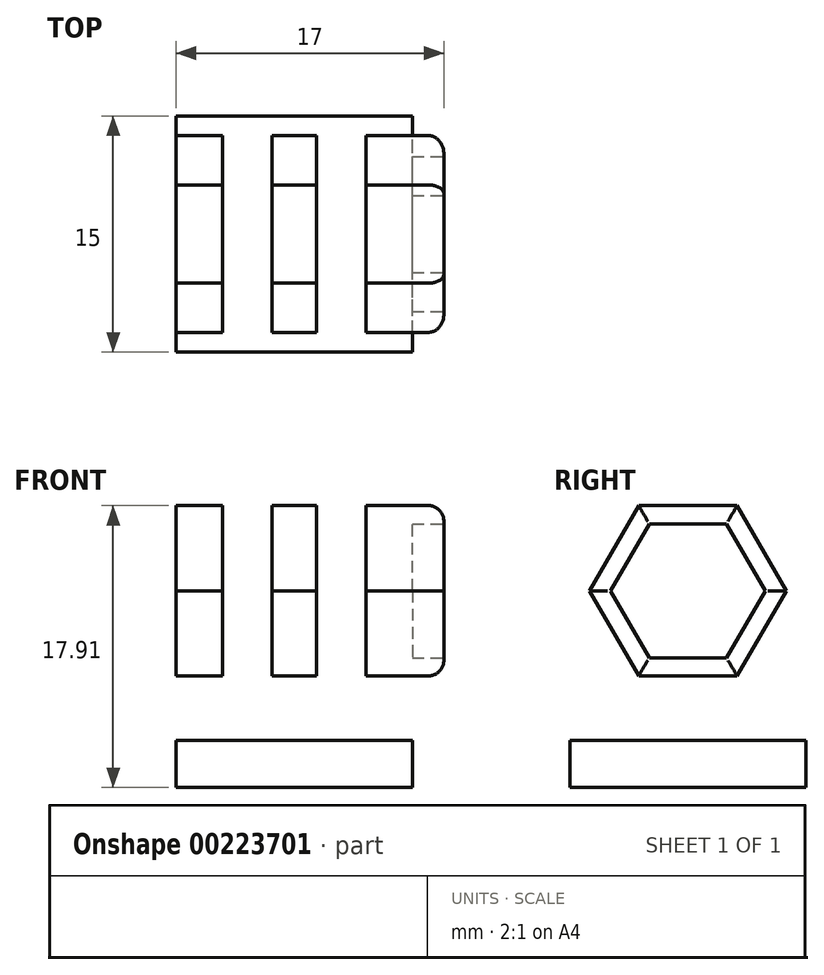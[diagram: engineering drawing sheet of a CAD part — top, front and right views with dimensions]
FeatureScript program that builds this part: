
annotation { "Feature Type Name" : "Feature", "Feature Type Description" : "" }
export const myFeature = defineFeature(function(context is Context, id is Id, definition is map)
    precondition{}
    {
        {
            var Q0;
            Q0=qCreatedBy(makeId("Right.planeOp"),FACE);
            var sketch = newSketch(context, id + "F0", { "sketchPlane" : qUnion([Q0])});
            skPoint(sketch, "E0", {"position": v(0, 12.5) * mm});
            skPoint(sketch, "E1", {"position": v(7.5, 0) * mm});
            skPoint(sketch, "E2.end.orphan", {"position": v(-7.5, 0) * mm});
            skLineSegment(sketch, "E3.top", {"start": v(-7.5, 0) * mm, "end": v(7.5, 0) * mm});
            skLineSegment(sketch, "E3.left", {"start": v(-7.5, 12.5) * mm, "end": v(-7.5, 0) * mm});
            skLineSegment(sketch, "E3.right", {"start": v(7.5, 12.5) * mm, "end": v(7.5, 0) * mm});
            skArc(sketch, "E4", {"start": v(7.5, 12.5) * mm, "mid": v(0, 20) * mm, "end": v(-7.5, 12.5) * mm});
            skCircle(sketch, "E5.cCircle", {"center": v(0, 12.5) * mm, "radius": 4.25 * mm, "construction": true});
            skLineSegment(sketch, "E5.0", {"start": v(-2.45, 16.75) * mm, "end": v(2.45, 16.75) * mm});
            skLineSegment(sketch, "E5.1", {"start": v(2.45, 16.75) * mm, "end": v(4.9, 12.5) * mm});
            skLineSegment(sketch, "E5.2", {"start": v(4.9, 12.5) * mm, "end": v(2.45, 8.25) * mm});
            skLineSegment(sketch, "E5.3", {"start": v(2.45, 8.25) * mm, "end": v(-2.45, 8.25) * mm});
            skLineSegment(sketch, "E5.4", {"start": v(-2.45, 8.25) * mm, "end": v(-4.9, 12.5) * mm});
            skLineSegment(sketch, "E5.5", {"start": v(-4.9, 12.5) * mm, "end": v(-2.45, 16.75) * mm});
            skPoint(sketch, "E5.0.midPoint", {"position": v(0, 16.75) * mm});
            skCircle(sketch, "E6.cCircle", {"center": v(0, 12.5) * mm, "radius": 5.41 * mm, "construction": true});
            skLineSegment(sketch, "E6.0", {"start": v(-3.12, 17.91) * mm, "end": v(3.12, 17.91) * mm});
            skLineSegment(sketch, "E6.1", {"start": v(3.12, 17.91) * mm, "end": v(6.25, 12.5) * mm});
            skLineSegment(sketch, "E6.2", {"start": v(6.25, 12.5) * mm, "end": v(3.12, 7.09) * mm});
            skLineSegment(sketch, "E6.3", {"start": v(3.13, 7.09) * mm, "end": v(-3.12, 7.09) * mm});
            skLineSegment(sketch, "E6.4", {"start": v(-3.12, 7.09) * mm, "end": v(-6.25, 12.5) * mm});
            skLineSegment(sketch, "E6.5", {"start": v(-6.25, 12.5) * mm, "end": v(-3.12, 17.91) * mm});
            skPoint(sketch, "E6.0.midPoint", {"position": v(0, 17.91) * mm});
            skLineSegment(sketch, "E7.top", {"start": v(-7.5, 3) * mm, "end": v(7.5, 3) * mm});
            skLineSegment(sketch, "E7.left", {"start": v(-7.5, 0) * mm, "end": v(-7.5, 3) * mm});
            skLineSegment(sketch, "E7.right", {"start": v(7.5, 0) * mm, "end": v(7.5, 3) * mm});
            skSolve(sketch);
        }
        {
            var Q0;
            Q0=makeQuery(id+"F0.imprint","IMPRINT",FACE,{"disambiguationData":[TD([[makeQuery(id+"F0.imprint","IMPRINT",EDGE,{"derivedFrom":sQuery(id+"F0.wireOp",EDGE,"E3.top")}),1.0]])]});
            extrude(context, id + "F1", {"entities" : qUnion([Q0]), "oppositeDirection" : true, "depth" : 15 * mm});
        }
        {
            var Q0;
            Q0=makeQuery(id+"F0.imprint","IMPRINT",FACE,{"disambiguationData":[TD([[makeQuery(id+"F0.imprint","IMPRINT",EDGE,{"derivedFrom":sQuery(id+"F0.wireOp",EDGE,"E3.left")}),1.0]])]});
            extrude(context, id + "F2", {"entities" : qUnion([Q0]), "operationType" : NewBodyOperationType.ADD, "oppositeDirection" : true, "depth" : 3 * mm});
        }
        {
            var Q0;
            Q0=makeQuery(id+"F0.imprint","IMPRINT",FACE,{"disambiguationData":[TD([[makeQuery(id+"F0.imprint","IMPRINT",EDGE,{"derivedFrom":sQuery(id+"F0.wireOp",EDGE,"E5.0")}),1.0]])]});
            extrude(context, id + "F3", {"entities" : qUnion([Q0]), "operationType" : NewBodyOperationType.ADD, "oppositeDirection" : true, "depth" : 3 * mm});
        }
        {
            var Q0;
            Q0=makeQuery(id+"F0.imprint","IMPRINT",FACE,{"disambiguationData":[TD([[makeQuery(id+"F0.imprint","IMPRINT",EDGE,{"derivedFrom":sQuery(id+"F0.wireOp",EDGE,"E5.0")}),1.0]])]});
            extrude(context, id + "F4", {"entities" : qUnion([Q0]), "operationType" : NewBodyOperationType.ADD, "depth" : 2 * mm});
        }
        {
            var Q0;
            Q0=makeQuery(id+"F0.imprint","IMPRINT",FACE,{"disambiguationData":[TD([[makeQuery(id+"F0.imprint","IMPRINT",EDGE,{"derivedFrom":sQuery(id+"F0.wireOp",EDGE,"E5.0")}),-1.0]])]});
            extrude(context, id + "F5", {"entities" : qUnion([Q0]), "operationType" : NewBodyOperationType.ADD, "oppositeDirection" : true, "depth" : 3 * mm});
        }
        {
            var Q0;
            {var subQ0=sQuery(id+"F0.wireOp",EDGE,"E5.5");var subQ1=sQuery(id+"F0.wireOp",EDGE,"E5.4");var subQ2=sQuery(id+"F0.wireOp",EDGE,"E5.3");var subQ3=sQuery(id+"F0.wireOp",EDGE,"E5.2");var subQ4=sQuery(id+"F0.wireOp",EDGE,"E5.1");var subQ5=sQuery(id+"F0.wireOp",EDGE,"E5.0");var subQ6=sQuery(id+"F0.wireOp",EDGE,"E6.5");var subQ7=sQuery(id+"F0.wireOp",EDGE,"E6.4");var subQ8=sQuery(id+"F0.wireOp",EDGE,"E6.3");var subQ9=sQuery(id+"F0.wireOp",EDGE,"E6.2");var subQ10=sQuery(id+"F0.wireOp",EDGE,"E6.1");var subQ11=sQuery(id+"F0.wireOp",EDGE,"E6.0");Q0=makeQuery(id+"F5.boolean.opBoolean","MERGE",FACE,{"derivedFrom":[makeQuery(id+"F3.boolean.opBoolean","MERGE",FACE,{"derivedFrom":[makeQuery(id+"F2.opExtrude","CAP_FACE",FACE,{"disambiguationData":[OSD([sQuery(id+"F0.wireOp",EDGE,"E3.left"),sQuery(id+"F0.wireOp",EDGE,"E3.right"),sQuery(id+"F0.wireOp",EDGE,"E4"),subQ11,subQ10,subQ9,subQ8,subQ7,subQ6,sQuery(id+"F0.wireOp",EDGE,"E7.top")])],"isStart":false}),makeQuery(id+"F3.opExtrude","CAP_FACE",FACE,{"disambiguationData":[OSD([subQ5,subQ4,subQ3,subQ2,subQ1,subQ0,subQ11,subQ10,subQ9,subQ8,subQ7,subQ6])],"isStart":false})]}),makeQuery(id+"F5.opExtrude","CAP_FACE",FACE,{"disambiguationData":[OSD([subQ5,subQ4,subQ3,subQ2,subQ1,subQ0])],"isStart":false})]});}
            extrude(context, id + "F6", {"entities" : qUnion([Q0]), "operationType" : NewBodyOperationType.ADD, "depth" : 12 * mm});
        }
        {
            var Q0;
            Q0=sQuery(id+"F0.wireOp",VERTEX,"E0");
            var Q1;
            Q1=makeQuery(id+"F1.opExtrude","SWEPT_BODY",BODY,{"disambiguationData":[OSD([sQuery(id+"F0.wireOp",EDGE,"E3.top"),sQuery(id+"F0.wireOp",EDGE,"E7.top"),sQuery(id+"F0.wireOp",EDGE,"E7.left"),sQuery(id+"F0.wireOp",EDGE,"E7.right")])]});
            hole(context, id + "F7", {"style" : HoleStyle.SIMPLE, "endStyle" : HoleEndStyle.BLIND, "holeDiameter" : 5 * mm, "holeDepth" : 15 * mm, "locations" : qUnion([Q0]), "scope" : qUnion([Q1])});
        }
        {
            var Q0;
            Q0=qCreatedBy(makeId("Top.planeOp"),FACE);
            cPlane(context, id + "F8", {"entities" : qUnion([Q0]), "cplaneType" : CPlaneType.OFFSET, "offset" : 20 * mm, "width" : 150 * mm, "height" : 150 * mm});
        }
        {
            var Q0;
            Q0=qCreatedBy(id+"F8.planeOp",FACE);
            var sketch = newSketch(context, id + "F9", { "sketchPlane" : qUnion([Q0])});
            skLineSegment(sketch, "E8.top", {"start": v(0, 7.5) * mm, "end": v(-15, 7.5) * mm});
            skLineSegment(sketch, "E8.left", {"start": v(0, 0) * mm, "end": v(0, 7.5) * mm});
            skLineSegment(sketch, "E8.right", {"start": v(-15, 0) * mm, "end": v(-15, 7.5) * mm});
            skLineSegment(sketch, "E9.top", {"start": v(-15, -7.5) * mm, "end": v(0, -7.5) * mm});
            skLineSegment(sketch, "E9.left", {"start": v(-15, 0) * mm, "end": v(-15, -7.5) * mm});
            skLineSegment(sketch, "E9.right", {"start": v(0, 0) * mm, "end": v(0, -7.5) * mm});
            skLineSegment(sketch, "E10", {"start": v(-7.5, -7.5) * mm, "end": v(-7.5, 7.5) * mm, "construction": true});
            skPoint(sketch, "E11", {"position": v(-6.1, -7.5) * mm});
            skLineSegment(sketch, "E12.bottom", {"start": v(-6.1, -7.5) * mm, "end": v(-8.9, -7.5) * mm});
            skLineSegment(sketch, "E12.top", {"start": v(-6.1, 7.5) * mm, "end": v(-8.9, 7.5) * mm});
            skLineSegment(sketch, "E12.left", {"start": v(-6.1, -7.5) * mm, "end": v(-6.1, 7.5) * mm});
            skLineSegment(sketch, "E12.right", {"start": v(-8.9, -7.5) * mm, "end": v(-8.9, 7.5) * mm});
            skLineSegment(sketch, "E13.bottom", {"start": v(-15, -7.5) * mm, "end": v(-12.05, -7.5) * mm});
            skLineSegment(sketch, "E13.top", {"start": v(-15, 7.5) * mm, "end": v(-12.05, 7.5) * mm});
            skLineSegment(sketch, "E13.left", {"start": v(-15, -7.5) * mm, "end": v(-15, 7.5) * mm});
            skLineSegment(sketch, "E13.right", {"start": v(-12.05, -7.5) * mm, "end": v(-12.05, 7.5) * mm});
            skLineSegment(sketch, "E14.bottom", {"start": v(0, -7.5) * mm, "end": v(-2.95, -7.5) * mm});
            skLineSegment(sketch, "E14.top", {"start": v(0, 7.5) * mm, "end": v(-2.95, 7.5) * mm});
            skLineSegment(sketch, "E14.left", {"start": v(0, -7.5) * mm, "end": v(0, 7.5) * mm});
            skLineSegment(sketch, "E14.right", {"start": v(-2.95, -7.5) * mm, "end": v(-2.95, 7.5) * mm});
            skSolve(sketch);
        }
        {
            var Q0;
            {var subQ2=sQuery(id+"F9.wireOp",EDGE,"E12.right");Q0=makeQuery(id+"F9.imprint","IMPRINT",FACE,{"disambiguationData":[TD([[makeQuery(id+"F9.imprint","IMPRINT",EDGE,{"derivedFrom":subQ2}),1.0]])]});}
            var Q1;
            {var subQ2=sQuery(id+"F9.wireOp",EDGE,"E12.left");Q1=makeQuery(id+"F9.imprint","IMPRINT",FACE,{"disambiguationData":[TD([[makeQuery(id+"F9.imprint","IMPRINT",EDGE,{"derivedFrom":subQ2}),-1.0]])]});}
            extrude(context, id + "F10", {"entities" : qUnion([Q0, Q1]), "operationType" : NewBodyOperationType.REMOVE, "oppositeDirection" : true, "depth" : 17 * mm});
        }
        {
            var Q0;
            Q0=makeQuery(id+"F4.opExtrude","CAP_EDGE",EDGE,{"disambiguationData":[OSD([sQuery(id+"F0.wireOp",EDGE,"E6.4")])],"isStart":false});
            var Q1;
            Q1=makeQuery(id+"F4.opExtrude","CAP_EDGE",EDGE,{"disambiguationData":[OSD([sQuery(id+"F0.wireOp",EDGE,"E6.3")])],"isStart":false});
            var Q2;
            Q2=makeQuery(id+"F4.opExtrude","CAP_EDGE",EDGE,{"disambiguationData":[OSD([sQuery(id+"F0.wireOp",EDGE,"E6.5")])],"isStart":false});
            var Q3;
            Q3=makeQuery(id+"F4.opExtrude","CAP_EDGE",EDGE,{"disambiguationData":[OSD([sQuery(id+"F0.wireOp",EDGE,"E6.0")])],"isStart":false});
            var Q4;
            Q4=makeQuery(id+"F4.opExtrude","CAP_EDGE",EDGE,{"disambiguationData":[OSD([sQuery(id+"F0.wireOp",EDGE,"E6.1")])],"isStart":false});
            var Q5;
            Q5=makeQuery(id+"F4.opExtrude","CAP_EDGE",EDGE,{"disambiguationData":[OSD([sQuery(id+"F0.wireOp",EDGE,"E6.2")])],"isStart":false});
            fillet(context, id + "F11", {"entities" : qUnion([Q0, Q1, Q2, Q3, Q4, Q5]), "radius" : 1 * mm, "tangentPropagation" : true, "allowEdgeOverflow" : false});
        }
    });
